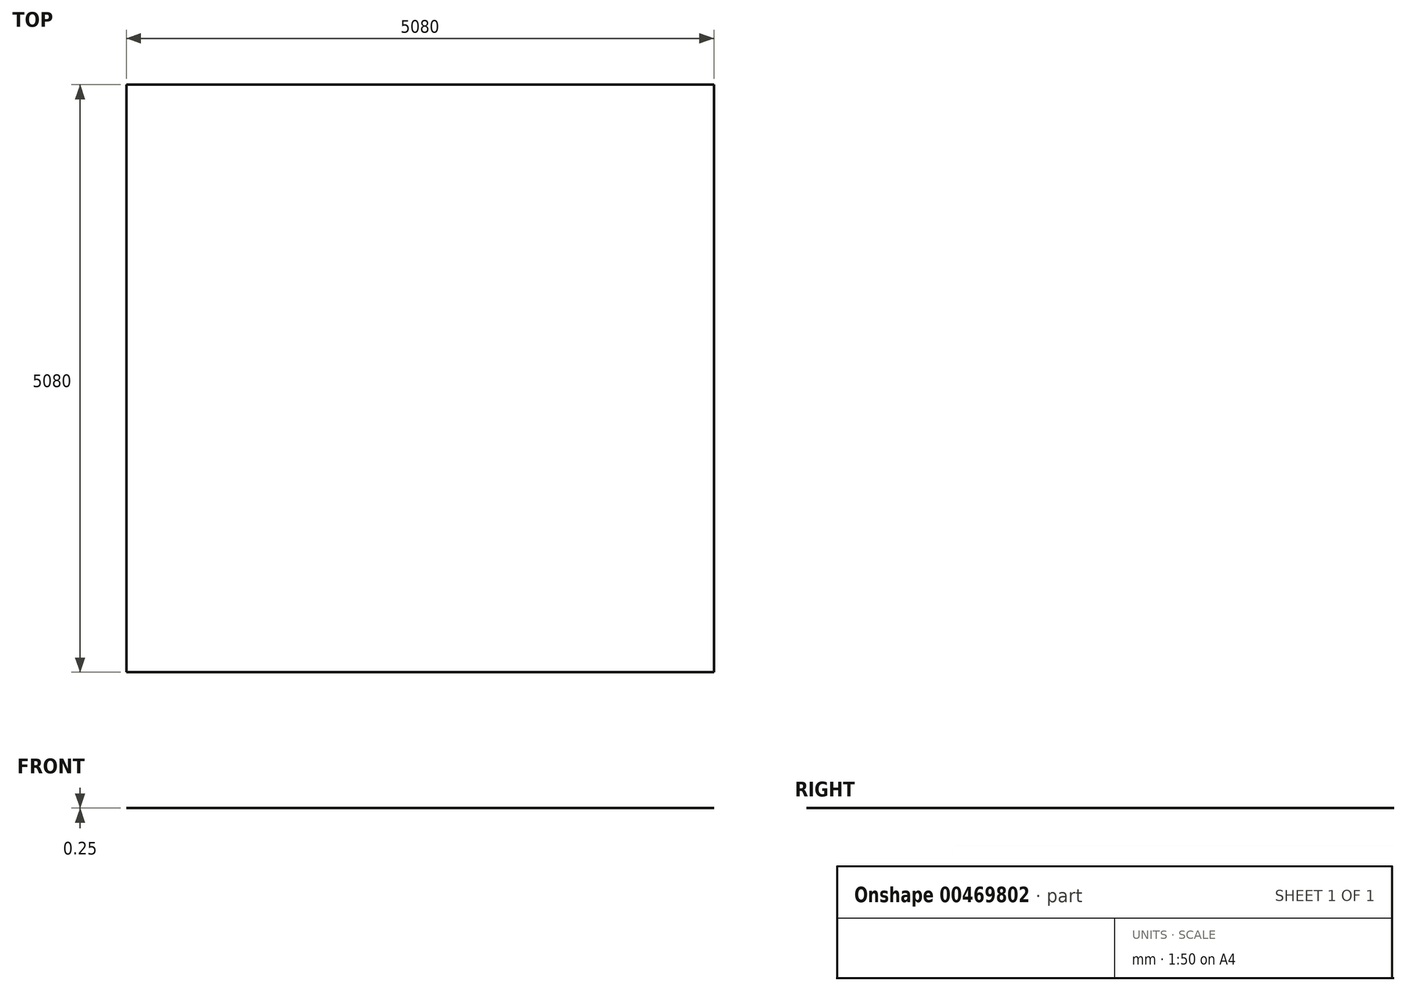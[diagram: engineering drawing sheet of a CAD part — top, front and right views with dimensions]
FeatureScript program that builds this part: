
annotation { "Feature Type Name" : "Feature", "Feature Type Description" : "" }
export const myFeature = defineFeature(function(context is Context, id is Id, definition is map)
    precondition{}
    {
        {
            var Q0;
            Q0=qCreatedBy(makeId("Top.planeOp"),FACE);
            var sketch = newSketch(context, id + "F0", { "sketchPlane" : qUnion([Q0])});
            skLineSegment(sketch, "E0.bottom", {"start": v(2540, -2540) * mm, "end": v(-2540, -2540) * mm});
            skLineSegment(sketch, "E0.top", {"start": v(2540, 2540) * mm, "end": v(-2540, 2540) * mm});
            skLineSegment(sketch, "E0.left", {"start": v(2540, -2540) * mm, "end": v(2540, 2540) * mm});
            skLineSegment(sketch, "E0.right", {"start": v(-2540, -2540) * mm, "end": v(-2540, 2540) * mm});
            skPoint(sketch, "E0.middle", {"position": v(0, 0) * mm});
            skSolve(sketch);
        }
        {
            var Q0;
            Q0=qSketchRegion(id+"F0",true);
            extrude(context, id + "F1", {"entities" : qUnion([Q0]), "depth" : 0.25 * mm});
        }
    });
